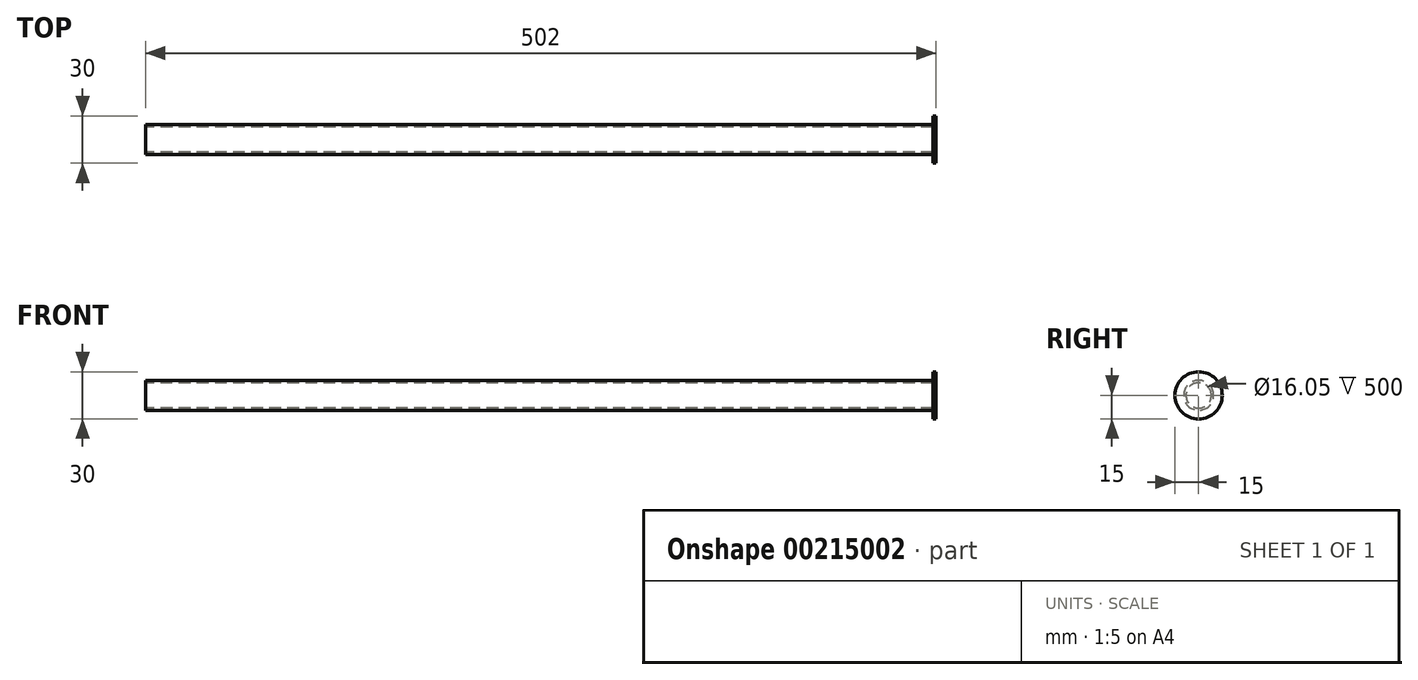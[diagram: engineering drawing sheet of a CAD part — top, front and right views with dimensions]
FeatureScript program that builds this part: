
annotation { "Feature Type Name" : "Feature", "Feature Type Description" : "" }
export const myFeature = defineFeature(function(context is Context, id is Id, definition is map)
    precondition{}
    {
        {
            var Q0;
            Q0=qCreatedBy(makeId("Front.planeOp"),FACE);
            var sketch = newSketch(context, id + "F0", { "sketchPlane" : qUnion([Q0])});
            skLineSegment(sketch, "E0", {"start": v(0, 0) * mm, "end": v(2, 0) * mm});
            skLineSegment(sketch, "E1", {"start": v(2, 0) * mm, "end": v(2, 15) * mm});
            skLineSegment(sketch, "E2", {"start": v(2, 15) * mm, "end": v(0, 15) * mm});
            skLineSegment(sketch, "E3", {"start": v(0, 15) * mm, "end": v(0, 9.53) * mm});
            skLineSegment(sketch, "E4", {"start": v(0, 9.53) * mm, "end": v(-500, 9.52) * mm});
            skLineSegment(sketch, "E5", {"start": v(-500, 9.52) * mm, "end": v(-500, 8.02) * mm});
            skLineSegment(sketch, "E6", {"start": v(-500, 8.02) * mm, "end": v(0, 8.03) * mm});
            skLineSegment(sketch, "E7", {"start": v(0, 8.03) * mm, "end": v(0, 0) * mm});
            skSolve(sketch);
        }
        {
            var Q0;
            Q0 = qSketchRegion(id + "F0", true);
            var Q1;
            Q1=sQuery(id+"F0.wireOp",EDGE,"E0");
            revolve(context, id + "F1", {"entities" : qUnion([Q0]), "axis" : qUnion([Q1]), "revolveType" : RevolveType.FULL});
        }
    });
